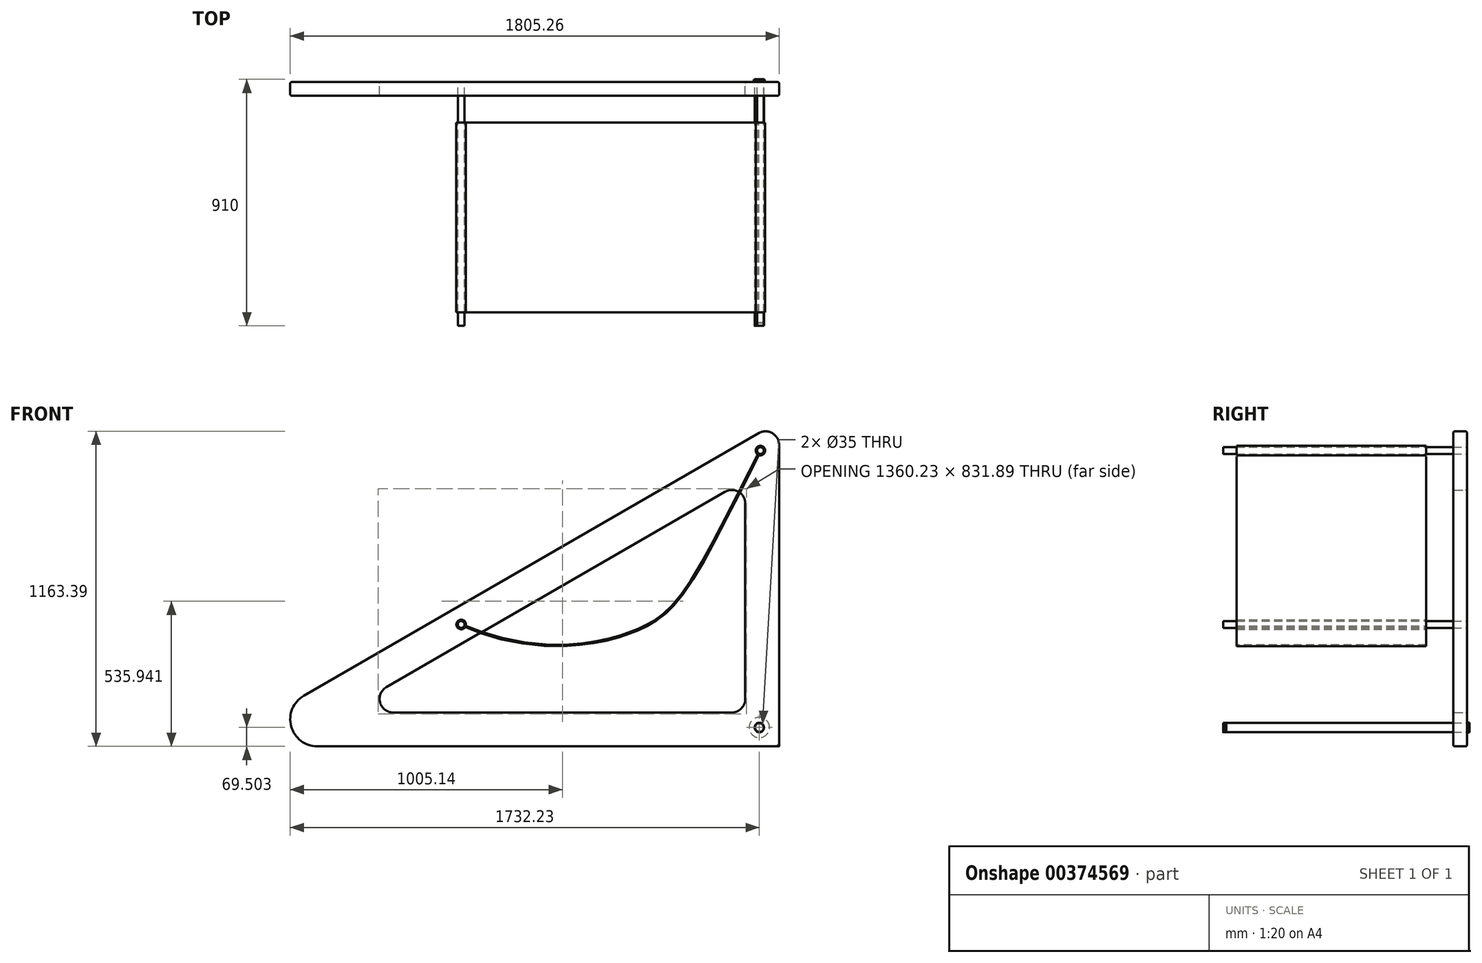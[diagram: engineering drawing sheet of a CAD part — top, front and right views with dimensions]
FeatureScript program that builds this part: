
annotation { "Feature Type Name" : "Feature", "Feature Type Description" : "" }
export const myFeature = defineFeature(function(context is Context, id is Id, definition is map)
    precondition{}
    {
        {
            var Q0;
            Q0=qCreatedBy(makeId("Front.planeOp"),FACE);
            var sketch = newSketch(context, id + "F0", { "sketchPlane" : qUnion([Q0])});
            skLineSegment(sketch, "E0.0", {"start": v(1202.53, -38.1) * mm, "end": v(2907.29, -38.1) * mm});
            skLineSegment(sketch, "E0.1", {"start": v(2832.79, 1118.6) * mm, "end": v(1152.53, 148.5) * mm});
            skLineSegment(sketch, "E0.2", {"start": v(2907.79, -37.6) * mm, "end": v(2907.79, 1075.3) * mm});
            skLineSegment(sketch, "E1.0", {"start": v(2782.79, 136.9) * mm, "end": v(2782.79, 858.8) * mm});
            skLineSegment(sketch, "E1.1", {"start": v(1482.43, 86.9) * mm, "end": v(2732.79, 86.9) * mm});
            skLineSegment(sketch, "E1.2", {"start": v(2707.79, 902.1) * mm, "end": v(1457.43, 180.2) * mm});
            skCircle(sketch, "E2", {"center": v(2838.8, 1054.2) * mm, "radius": 12.5 * mm});
            skCircle(sketch, "E3", {"center": v(2834.76, 31.41) * mm, "radius": 17.5 * mm});
            skCircle(sketch, "E4", {"center": v(1733.75, 411.9) * mm, "radius": 12.5 * mm});
            skCircle(sketch, "E5.cCircle", {"center": v(2838.8, 1054.2) * mm, "radius": 12.5 * mm, "construction": true});
            skLineSegment(sketch, "E5.0", {"start": v(2824.76, 1050.86) * mm, "end": v(2828.89, 1064.69) * mm});
            skLineSegment(sketch, "E5.1", {"start": v(2828.89, 1064.69) * mm, "end": v(2842.93, 1068.03) * mm});
            skLineSegment(sketch, "E5.2", {"start": v(2842.93, 1068.03) * mm, "end": v(2852.84, 1057.54) * mm});
            skLineSegment(sketch, "E5.3", {"start": v(2852.84, 1057.54) * mm, "end": v(2848.72, 1043.7) * mm});
            skLineSegment(sketch, "E5.4", {"start": v(2848.72, 1043.7) * mm, "end": v(2834.68, 1040.37) * mm});
            skLineSegment(sketch, "E5.5", {"start": v(2834.68, 1040.37) * mm, "end": v(2824.76, 1050.86) * mm});
            skPoint(sketch, "E5.0.midPoint", {"position": v(2826.82, 1057.77) * mm});
            skCircle(sketch, "E6.cCircle", {"center": v(2834.76, 31.41) * mm, "radius": 17.5 * mm, "construction": true});
            skLineSegment(sketch, "E6.0", {"start": v(2814.58, 30.3) * mm, "end": v(2823.7, 48.33) * mm});
            skLineSegment(sketch, "E6.1", {"start": v(2823.7, 48.33) * mm, "end": v(2843.88, 49.44) * mm});
            skLineSegment(sketch, "E6.2", {"start": v(2843.88, 49.44) * mm, "end": v(2854.93, 32.53) * mm});
            skLineSegment(sketch, "E6.3", {"start": v(2854.93, 32.53) * mm, "end": v(2845.81, 14.5) * mm});
            skLineSegment(sketch, "E6.4", {"start": v(2845.81, 14.5) * mm, "end": v(2825.63, 13.38) * mm});
            skLineSegment(sketch, "E6.5", {"start": v(2825.63, 13.38) * mm, "end": v(2814.58, 30.3) * mm});
            skPoint(sketch, "E6.0.midPoint", {"position": v(2819.14, 39.31) * mm});
            skCircle(sketch, "E7.cCircle", {"center": v(1733.75, 411.9) * mm, "radius": 12.5 * mm, "construction": true});
            skLineSegment(sketch, "E7.0", {"start": v(1721.66, 419.79) * mm, "end": v(1734.53, 426.32) * mm});
            skLineSegment(sketch, "E7.1", {"start": v(1734.53, 426.32) * mm, "end": v(1746.62, 418.43) * mm});
            skLineSegment(sketch, "E7.2", {"start": v(1746.62, 418.43) * mm, "end": v(1745.84, 404.02) * mm});
            skLineSegment(sketch, "E7.3", {"start": v(1745.84, 404.02) * mm, "end": v(1732.96, 397.5) * mm});
            skLineSegment(sketch, "E7.4", {"start": v(1732.96, 397.5) * mm, "end": v(1720.87, 405.38) * mm});
            skLineSegment(sketch, "E7.5", {"start": v(1720.87, 405.38) * mm, "end": v(1721.66, 419.79) * mm});
            skPoint(sketch, "E7.0.midPoint", {"position": v(1728.1, 423.05) * mm});
            skCircle(sketch, "E8", {"center": v(1733.75, 411.9) * mm, "radius": 37.5 * mm});
            skCircle(sketch, "E9", {"center": v(2838.8, 1054.2) * mm, "radius": 37.5 * mm});
            skCircle(sketch, "E10", {"center": v(2834.76, 31.41) * mm, "radius": 37.5 * mm});
            skPoint(sketch, "E11.visualSharp", {"position": v(829.32, -38.1) * mm});
            skArc(sketch, "E11.filletArc", {"start": v(1152.53, 148.5) * mm, "mid": v(1105.94, 36.02) * mm, "end": v(1202.53, -38.1) * mm});
            skPoint(sketch, "E12.visualSharp", {"position": v(1295.83, 86.9) * mm});
            skArc(sketch, "E12.filletArc", {"start": v(1457.43, 180.2) * mm, "mid": v(1434.14, 123.96) * mm, "end": v(1482.43, 86.9) * mm});
            skPoint(sketch, "E13.visualSharp", {"position": v(2782.79, 945.4) * mm});
            skArc(sketch, "E13.filletArc", {"start": v(2782.79, 858.8) * mm, "mid": v(2757.79, 902.1) * mm, "end": v(2707.79, 902.1) * mm});
            skPoint(sketch, "E14.visualSharp", {"position": v(2907.79, 1161.9) * mm});
            skArc(sketch, "E14.filletArc", {"start": v(2907.79, 1075.3) * mm, "mid": v(2882.79, 1118.6) * mm, "end": v(2832.79, 1118.6) * mm});
            skPoint(sketch, "E15.visualSharp", {"position": v(2782.79, 86.9) * mm});
            skArc(sketch, "E15.filletArc", {"start": v(2732.79, 86.9) * mm, "mid": v(2768.14, 101.55) * mm, "end": v(2782.79, 136.9) * mm});
            skPoint(sketch, "E16.visualSharp", {"position": v(2907.79, -38.1) * mm});
            skArc(sketch, "E16.filletArc", {"start": v(2907.29, -38.1) * mm, "mid": v(2907.64, -37.95) * mm, "end": v(2907.79, -37.6) * mm});
            skSolve(sketch);
        }
        {
            var Q0;
            Q0=makeQuery(id+"F0.imprint","IMPRINT",FACE,{"disambiguationData":[TD([[makeQuery(id+"F0.imprint","IMPRINT",EDGE,{"derivedFrom":sQuery(id+"F0.wireOp",EDGE,"E0.0")}),1.0]])]});
            var Q1;
            Q1=makeQuery(id+"F0.imprint","IMPRINT",FACE,{"disambiguationData":[TD([[makeQuery(id+"F0.imprint","IMPRINT",EDGE,{"derivedFrom":sQuery(id+"F0.wireOp",EDGE,"E9")}),1.0]])]});
            var Q2;
            {var subQ0=sQuery(id+"F0.wireOp",EDGE,"E5.4");var subQ1=sQuery(id+"F0.wireOp",EDGE,"E2");var subQ2=makeQuery(id+"F0.imprint","INTERSECT",VERTEX,{"derivedFrom":[subQ1,subQ0]});Q2=makeQuery(id+"F0.imprint","IMPRINT",FACE,{"disambiguationData":[TD([[makeQuery(id+"F0.imprint","IMPRINT",EDGE,{"disambiguationData":[TD([[subQ2,-1.0]])],"derivedFrom":subQ1}),-1.0]])]});}
            var Q3;
            {var subQ0=sQuery(id+"F0.wireOp",EDGE,"E5.2");var subQ1=sQuery(id+"F0.wireOp",EDGE,"E2");var subQ2=makeQuery(id+"F0.imprint","INTERSECT",VERTEX,{"derivedFrom":[subQ1,subQ0]});Q3=makeQuery(id+"F0.imprint","IMPRINT",FACE,{"disambiguationData":[TD([[makeQuery(id+"F0.imprint","IMPRINT",EDGE,{"disambiguationData":[TD([[subQ2,1.0]])],"derivedFrom":subQ1}),-1.0]])]});}
            var Q4;
            {var subQ0=sQuery(id+"F0.wireOp",EDGE,"E5.5");var subQ1=sQuery(id+"F0.wireOp",EDGE,"E2");var subQ2=makeQuery(id+"F0.imprint","INTERSECT",VERTEX,{"derivedFrom":[subQ1,subQ0]});Q4=makeQuery(id+"F0.imprint","IMPRINT",FACE,{"disambiguationData":[TD([[makeQuery(id+"F0.imprint","IMPRINT",EDGE,{"disambiguationData":[TD([[subQ2,-1.0]])],"derivedFrom":subQ1}),-1.0]])]});}
            var Q5;
            {var subQ0=sQuery(id+"F0.wireOp",EDGE,"E5.0");var subQ1=sQuery(id+"F0.wireOp",EDGE,"E2");var subQ2=makeQuery(id+"F0.imprint","INTERSECT",VERTEX,{"derivedFrom":[subQ1,subQ0]});Q5=makeQuery(id+"F0.imprint","IMPRINT",FACE,{"disambiguationData":[TD([[makeQuery(id+"F0.imprint","IMPRINT",EDGE,{"disambiguationData":[TD([[subQ2,-1.0]])],"derivedFrom":subQ1}),-1.0]])]});}
            var Q6;
            {var subQ0=sQuery(id+"F0.wireOp",EDGE,"E5.1");var subQ1=sQuery(id+"F0.wireOp",EDGE,"E2");var subQ2=makeQuery(id+"F0.imprint","INTERSECT",VERTEX,{"derivedFrom":[subQ1,subQ0]});Q6=makeQuery(id+"F0.imprint","IMPRINT",FACE,{"disambiguationData":[TD([[makeQuery(id+"F0.imprint","IMPRINT",EDGE,{"disambiguationData":[TD([[subQ2,-1.0]])],"derivedFrom":subQ1}),-1.0]])]});}
            var Q7;
            {var subQ0=sQuery(id+"F0.wireOp",EDGE,"E5.1");var subQ1=sQuery(id+"F0.wireOp",EDGE,"E2");var subQ2=makeQuery(id+"F0.imprint","INTERSECT",VERTEX,{"derivedFrom":[subQ1,subQ0]});Q7=makeQuery(id+"F0.imprint","IMPRINT",FACE,{"disambiguationData":[TD([[makeQuery(id+"F0.imprint","IMPRINT",EDGE,{"disambiguationData":[TD([[subQ2,1.0]])],"derivedFrom":subQ1}),-1.0]])]});}
            var Q8;
            Q8=makeQuery(id+"F0.imprint","IMPRINT",FACE,{"disambiguationData":[TD([[makeQuery(id+"F0.imprint","IMPRINT",EDGE,{"derivedFrom":sQuery(id+"F0.wireOp",EDGE,"E10")}),1.0]])]});
            var Q9;
            {var subQ0=sQuery(id+"F0.wireOp",EDGE,"E6.2");var subQ1=sQuery(id+"F0.wireOp",EDGE,"E3");var subQ2=makeQuery(id+"F0.imprint","INTERSECT",VERTEX,{"derivedFrom":[subQ1,subQ0]});Q9=makeQuery(id+"F0.imprint","IMPRINT",FACE,{"disambiguationData":[TD([[makeQuery(id+"F0.imprint","IMPRINT",EDGE,{"disambiguationData":[TD([[subQ2,1.0]])],"derivedFrom":subQ1}),-1.0]])]});}
            var Q10;
            {var subQ0=sQuery(id+"F0.wireOp",EDGE,"E6.1");var subQ1=sQuery(id+"F0.wireOp",EDGE,"E3");var subQ2=makeQuery(id+"F0.imprint","INTERSECT",VERTEX,{"derivedFrom":[subQ1,subQ0]});Q10=makeQuery(id+"F0.imprint","IMPRINT",FACE,{"disambiguationData":[TD([[makeQuery(id+"F0.imprint","IMPRINT",EDGE,{"disambiguationData":[TD([[subQ2,-1.0]])],"derivedFrom":subQ1}),-1.0]])]});}
            var Q11;
            {var subQ0=sQuery(id+"F0.wireOp",EDGE,"E6.1");var subQ1=sQuery(id+"F0.wireOp",EDGE,"E3");var subQ2=makeQuery(id+"F0.imprint","INTERSECT",VERTEX,{"derivedFrom":[subQ1,subQ0]});Q11=makeQuery(id+"F0.imprint","IMPRINT",FACE,{"disambiguationData":[TD([[makeQuery(id+"F0.imprint","IMPRINT",EDGE,{"disambiguationData":[TD([[subQ2,1.0]])],"derivedFrom":subQ1}),-1.0]])]});}
            var Q12;
            {var subQ0=sQuery(id+"F0.wireOp",EDGE,"E6.4");var subQ1=sQuery(id+"F0.wireOp",EDGE,"E3");var subQ2=makeQuery(id+"F0.imprint","INTERSECT",VERTEX,{"derivedFrom":[subQ1,subQ0]});Q12=makeQuery(id+"F0.imprint","IMPRINT",FACE,{"disambiguationData":[TD([[makeQuery(id+"F0.imprint","IMPRINT",EDGE,{"disambiguationData":[TD([[subQ2,-1.0]])],"derivedFrom":subQ1}),-1.0]])]});}
            var Q13;
            {var subQ0=sQuery(id+"F0.wireOp",EDGE,"E6.5");var subQ1=sQuery(id+"F0.wireOp",EDGE,"E3");var subQ2=makeQuery(id+"F0.imprint","INTERSECT",VERTEX,{"derivedFrom":[subQ1,subQ0]});Q13=makeQuery(id+"F0.imprint","IMPRINT",FACE,{"disambiguationData":[TD([[makeQuery(id+"F0.imprint","IMPRINT",EDGE,{"disambiguationData":[TD([[subQ2,-1.0]])],"derivedFrom":subQ1}),-1.0]])]});}
            var Q14;
            {var subQ0=sQuery(id+"F0.wireOp",EDGE,"E6.0");var subQ1=sQuery(id+"F0.wireOp",EDGE,"E3");var subQ2=makeQuery(id+"F0.imprint","INTERSECT",VERTEX,{"derivedFrom":[subQ1,subQ0]});Q14=makeQuery(id+"F0.imprint","IMPRINT",FACE,{"disambiguationData":[TD([[makeQuery(id+"F0.imprint","IMPRINT",EDGE,{"disambiguationData":[TD([[subQ2,-1.0]])],"derivedFrom":subQ1}),-1.0]])]});}
            var Q15;
            Q15=makeQuery(id+"F0.imprint","IMPRINT",FACE,{"disambiguationData":[TD([[makeQuery(id+"F0.imprint","IMPRINT",EDGE,{"derivedFrom":sQuery(id+"F0.wireOp",EDGE,"E8")}),1.0]])]});
            var Q16;
            {var subQ0=sQuery(id+"F0.wireOp",EDGE,"E7.0");var subQ1=sQuery(id+"F0.wireOp",EDGE,"E4");var subQ2=makeQuery(id+"F0.imprint","INTERSECT",VERTEX,{"derivedFrom":[subQ1,subQ0]});Q16=makeQuery(id+"F0.imprint","IMPRINT",FACE,{"disambiguationData":[TD([[makeQuery(id+"F0.imprint","IMPRINT",EDGE,{"disambiguationData":[TD([[subQ2,1.0]])],"derivedFrom":subQ1}),-1.0]])]});}
            var Q17;
            {var subQ0=sQuery(id+"F0.wireOp",EDGE,"E7.3");var subQ1=sQuery(id+"F0.wireOp",EDGE,"E4");var subQ2=makeQuery(id+"F0.imprint","INTERSECT",VERTEX,{"derivedFrom":[subQ1,subQ0]});Q17=makeQuery(id+"F0.imprint","IMPRINT",FACE,{"disambiguationData":[TD([[makeQuery(id+"F0.imprint","IMPRINT",EDGE,{"disambiguationData":[TD([[subQ2,-1.0]])],"derivedFrom":subQ1}),-1.0]])]});}
            var Q18;
            {var subQ0=sQuery(id+"F0.wireOp",EDGE,"E7.1");var subQ1=sQuery(id+"F0.wireOp",EDGE,"E4");var subQ2=makeQuery(id+"F0.imprint","INTERSECT",VERTEX,{"derivedFrom":[subQ1,subQ0]});Q18=makeQuery(id+"F0.imprint","IMPRINT",FACE,{"disambiguationData":[TD([[makeQuery(id+"F0.imprint","IMPRINT",EDGE,{"disambiguationData":[TD([[subQ2,1.0]])],"derivedFrom":subQ1}),-1.0]])]});}
            var Q19;
            {var subQ0=sQuery(id+"F0.wireOp",EDGE,"E7.4");var subQ1=sQuery(id+"F0.wireOp",EDGE,"E4");var subQ2=makeQuery(id+"F0.imprint","INTERSECT",VERTEX,{"derivedFrom":[subQ1,subQ0]});Q19=makeQuery(id+"F0.imprint","IMPRINT",FACE,{"disambiguationData":[TD([[makeQuery(id+"F0.imprint","IMPRINT",EDGE,{"disambiguationData":[TD([[subQ2,-1.0]])],"derivedFrom":subQ1}),-1.0]])]});}
            var Q20;
            {var subQ0=sQuery(id+"F0.wireOp",EDGE,"E7.0");var subQ1=sQuery(id+"F0.wireOp",EDGE,"E4");var subQ2=makeQuery(id+"F0.imprint","INTERSECT",VERTEX,{"derivedFrom":[subQ1,subQ0]});Q20=makeQuery(id+"F0.imprint","IMPRINT",FACE,{"disambiguationData":[TD([[makeQuery(id+"F0.imprint","IMPRINT",EDGE,{"disambiguationData":[TD([[subQ2,-1.0]])],"derivedFrom":subQ1}),-1.0]])]});}
            var Q21;
            {var subQ0=sQuery(id+"F0.wireOp",EDGE,"E7.5");var subQ1=sQuery(id+"F0.wireOp",EDGE,"E4");var subQ2=makeQuery(id+"F0.imprint","INTERSECT",VERTEX,{"derivedFrom":[subQ1,subQ0]});Q21=makeQuery(id+"F0.imprint","IMPRINT",FACE,{"disambiguationData":[TD([[makeQuery(id+"F0.imprint","IMPRINT",EDGE,{"disambiguationData":[TD([[subQ2,-1.0]])],"derivedFrom":subQ1}),-1.0]])]});}
            extrude(context, id + "F1", {"entities" : qUnion([Q0, Q1, Q2, Q3, Q4, Q5, Q6, Q7, Q8, Q9, Q10, Q11, Q12, Q13, Q14, Q15, Q16, Q17, Q18, Q19, Q20, Q21]), "depth" : 50 * mm});
        }
        {
            var Q0;
            Q0=makeQuery(id+"F0.imprint","IMPRINT",FACE,{"disambiguationData":[TD([[makeQuery(id+"F0.imprint","IMPRINT",EDGE,{"derivedFrom":sQuery(id+"F0.wireOp",EDGE,"E2")}),1.0]])]});
            var Q1;
            Q1=makeQuery(id+"F0.imprint","IMPRINT",FACE,{"disambiguationData":[TD([[makeQuery(id+"F0.imprint","IMPRINT",EDGE,{"derivedFrom":sQuery(id+"F0.wireOp",EDGE,"E3")}),1.0]])]});
            var Q2;
            Q2=makeQuery(id+"F0.imprint","IMPRINT",FACE,{"disambiguationData":[TD([[makeQuery(id+"F0.imprint","IMPRINT",EDGE,{"derivedFrom":sQuery(id+"F0.wireOp",EDGE,"E4")}),1.0]])]});
            extrude(context, id + "F2", {"entities" : qUnion([Q0, Q1, Q2]), "depth" : 25 * 36 * mm});
        }
        {
            var Q0;
            Q0=makeQuery(id+"F1.opExtrude","CAP_FACE",FACE,{"disambiguationData":[OSD([sQuery(id+"F0.wireOp",EDGE,"E0.0"),sQuery(id+"F0.wireOp",EDGE,"E0.1"),sQuery(id+"F0.wireOp",EDGE,"E0.2"),sQuery(id+"F0.wireOp",EDGE,"E1.0"),sQuery(id+"F0.wireOp",EDGE,"E1.1"),sQuery(id+"F0.wireOp",EDGE,"E1.2"),sQuery(id+"F0.wireOp",EDGE,"E2"),sQuery(id+"F0.wireOp",EDGE,"E3"),sQuery(id+"F0.wireOp",EDGE,"E4")])],"isStart":false});
            var sketch = newSketch(context, id + "F3", { "sketchPlane" : qUnion([Q0])});
            skFitSpline(sketch, "E17", {"points": [v(1733.75, 411.9) * mm, v(2383.9, 392.1) * mm, v(2838.8, 1054.2) * mm], "startDerivative": vector(1756.38, -743.3) * mm, "endDerivative": vector(1453.35, 2857.32) * mm});
            skCircle(sketch, "E18", {"center": v(1733.75, 411.9) * mm, "radius": 12.73 * mm});
            skCircle(sketch, "E19", {"center": v(2838.8, 1054.2) * mm, "radius": 12.64 * mm});
            skCircle(sketch, "E20.0", {"center": v(1733.75, 411.9) * mm, "radius": 17.73 * mm});
            skFitSpline(sketch, "E21.0", {"points": [v(1732.77, 409.6) * mm, v(1769.45, 394.08) * mm, v(1841.23, 368.44) * mm, v(1943.57, 344.38) * mm, v(2039.9, 332.88) * mm, v(2114.66, 332.24) * mm, v(2170.83, 336.19) * mm, v(2211.05, 341.14) * mm, v(2249.3, 347.86) * mm, v(2285.48, 356.12) * mm, v(2319.52, 365.7) * mm, v(2346.04, 374.57) * mm, v(2366.1, 382.1) * mm, v(2380.58, 387.93) * mm, v(2394.45, 393.9) * mm, v(2412.2, 402.13) * mm, v(2433.13, 413.04) * mm, v(2456.63, 427.63) * mm, v(2478.9, 444.17) * mm, v(2500.34, 463.15) * mm, v(2521.33, 485) * mm, v(2549.28, 518.63) * mm, v(2585.15, 570.22) * mm, v(2632.98, 651.24) * mm, v(2688.9, 755.21) * mm, v(2756.16, 885.96) * mm, v(2810.75, 993.54) * mm, v(2841.03, 1053.07) * mm]});
            skFitSpline(sketch, "E22.0", {"points": [v(1734.72, 414.2) * mm, v(1771.23, 398.76) * mm, v(1842.66, 373.25) * mm, v(1944.45, 349.31) * mm, v(2040.23, 337.88) * mm, v(2114.53, 337.25) * mm, v(2170.35, 341.17) * mm, v(2210.31, 346.09) * mm, v(2248.3, 352.77) * mm, v(2284.24, 360.97) * mm, v(2318.05, 370.47) * mm, v(2344.38, 379.29) * mm, v(2364.3, 386.76) * mm, v(2376.26, 391.58) * mm, v(2385.53, 395.5) * mm, v(2394.6, 399.5) * mm, v(2405.6, 404.58) * mm, v(2418.26, 410.93) * mm, v(2434.52, 419.8) * mm, v(2453.82, 431.77) * mm, v(2475.74, 448.06) * mm, v(2496.86, 466.75) * mm, v(2517.6, 488.33) * mm, v(2545.26, 521.61) * mm, v(2580.9, 572.88) * mm, v(2628.6, 653.67) * mm, v(2684.46, 757.52) * mm, v(2751.7, 888.23) * mm, v(2806.3, 995.8) * mm, v(2836.57, 1055.33) * mm]});
            skCircle(sketch, "E23.0", {"center": v(2838.8, 1054.2) * mm, "radius": 17.64 * mm});
            skSolve(sketch);
        }
        {
            var Q0;
            Q0 = qSketchRegion(id + "F3", true);
            extrude(context, id + "F4", {"entities" : qUnion([Q0]), "depth" : (25 * 32) * mm});
        }
        {
            var Q0;
            Q0 = qSketchRegion(id + "F3", true);
            extrude(context, id + "F5", {"entities" : qUnion([Q0]), "operationType" : NewBodyOperationType.REMOVE, "depth" : 100 * mm});
        }
        {
            var Q0;
            Q0=makeQuery(id+"F0.imprint","IMPRINT",FACE,{"disambiguationData":[TD([[makeQuery(id+"F0.imprint","IMPRINT",EDGE,{"derivedFrom":sQuery(id+"F0.wireOp",EDGE,"E10")}),1.0]])]});
            var Q1;
            Q1=makeQuery(id+"F2.opExtrude","CAP_FACE",FACE,{"disambiguationData":[OSD([sQuery(id+"F0.wireOp",EDGE,"E3")])],"isStart":true});
            var Q2;
            {var subQ0=sQuery(id+"F0.wireOp",EDGE,"E6.1");var subQ1=sQuery(id+"F0.wireOp",EDGE,"E3");var subQ2=makeQuery(id+"F0.imprint","INTERSECT",VERTEX,{"derivedFrom":[subQ1,subQ0]});Q2=makeQuery(id+"F0.imprint","IMPRINT",FACE,{"disambiguationData":[TD([[makeQuery(id+"F0.imprint","IMPRINT",EDGE,{"disambiguationData":[TD([[subQ2,1.0]])],"derivedFrom":subQ1}),-1.0]])]});}
            var Q3;
            {var subQ0=sQuery(id+"F0.wireOp",EDGE,"E6.4");var subQ1=sQuery(id+"F0.wireOp",EDGE,"E3");var subQ2=makeQuery(id+"F0.imprint","INTERSECT",VERTEX,{"derivedFrom":[subQ1,subQ0]});Q3=makeQuery(id+"F0.imprint","IMPRINT",FACE,{"disambiguationData":[TD([[makeQuery(id+"F0.imprint","IMPRINT",EDGE,{"disambiguationData":[TD([[subQ2,-1.0]])],"derivedFrom":subQ1}),-1.0]])]});}
            var Q4;
            {var subQ0=sQuery(id+"F0.wireOp",EDGE,"E6.1");var subQ1=sQuery(id+"F0.wireOp",EDGE,"E3");var subQ2=makeQuery(id+"F0.imprint","INTERSECT",VERTEX,{"derivedFrom":[subQ1,subQ0]});Q4=makeQuery(id+"F0.imprint","IMPRINT",FACE,{"disambiguationData":[TD([[makeQuery(id+"F0.imprint","IMPRINT",EDGE,{"disambiguationData":[TD([[subQ2,-1.0]])],"derivedFrom":subQ1}),-1.0]])]});}
            var Q5;
            {var subQ0=sQuery(id+"F0.wireOp",EDGE,"E6.0");var subQ1=sQuery(id+"F0.wireOp",EDGE,"E3");var subQ2=makeQuery(id+"F0.imprint","INTERSECT",VERTEX,{"derivedFrom":[subQ1,subQ0]});Q5=makeQuery(id+"F0.imprint","IMPRINT",FACE,{"disambiguationData":[TD([[makeQuery(id+"F0.imprint","IMPRINT",EDGE,{"disambiguationData":[TD([[subQ2,-1.0]])],"derivedFrom":subQ1}),-1.0]])]});}
            var Q6;
            {var subQ0=sQuery(id+"F0.wireOp",EDGE,"E6.2");var subQ1=sQuery(id+"F0.wireOp",EDGE,"E3");var subQ2=makeQuery(id+"F0.imprint","INTERSECT",VERTEX,{"derivedFrom":[subQ1,subQ0]});Q6=makeQuery(id+"F0.imprint","IMPRINT",FACE,{"disambiguationData":[TD([[makeQuery(id+"F0.imprint","IMPRINT",EDGE,{"disambiguationData":[TD([[subQ2,1.0]])],"derivedFrom":subQ1}),-1.0]])]});}
            var Q7;
            Q7=makeQuery(id+"F2.opExtrude","CAP_FACE",FACE,{"disambiguationData":[OSD([sQuery(id+"F0.wireOp",EDGE,"E3")])],"isStart":false});
            var Q8;
            {var subQ0=sQuery(id+"F0.wireOp",EDGE,"E6.5");var subQ1=sQuery(id+"F0.wireOp",EDGE,"E3");var subQ2=makeQuery(id+"F0.imprint","INTERSECT",VERTEX,{"derivedFrom":[subQ1,subQ0]});Q8=makeQuery(id+"F0.imprint","IMPRINT",FACE,{"disambiguationData":[TD([[makeQuery(id+"F0.imprint","IMPRINT",EDGE,{"disambiguationData":[TD([[subQ2,-1.0]])],"derivedFrom":subQ1}),-1.0]])]});}
            extrude(context, id + "F6", {"entities" : qUnion([Q0, Q1, Q2, Q3, Q4, Q5, Q6, Q7, Q8]), "oppositeDirection" : true, "depth" : 1 * mm});
        }
        {
            var Q0;
            {var subQ0=sQuery(id+"F0.wireOp",EDGE,"E6.4");var subQ1=sQuery(id+"F0.wireOp",EDGE,"E3");var subQ2=makeQuery(id+"F0.imprint","INTERSECT",VERTEX,{"derivedFrom":[subQ1,subQ0]});Q0=makeQuery(id+"F0.imprint","IMPRINT",FACE,{"disambiguationData":[TD([[makeQuery(id+"F0.imprint","IMPRINT",EDGE,{"disambiguationData":[TD([[subQ2,-1.0]])],"derivedFrom":subQ1}),-1.0]])]});}
            var Q1;
            {var subQ0=sQuery(id+"F0.wireOp",EDGE,"E6.2");var subQ1=sQuery(id+"F0.wireOp",EDGE,"E3");var subQ2=makeQuery(id+"F0.imprint","INTERSECT",VERTEX,{"derivedFrom":[subQ1,subQ0]});Q1=makeQuery(id+"F0.imprint","IMPRINT",FACE,{"disambiguationData":[TD([[makeQuery(id+"F0.imprint","IMPRINT",EDGE,{"disambiguationData":[TD([[subQ2,1.0]])],"derivedFrom":subQ1}),-1.0]])]});}
            var Q2;
            {var subQ0=sQuery(id+"F0.wireOp",EDGE,"E6.1");var subQ1=sQuery(id+"F0.wireOp",EDGE,"E3");var subQ2=makeQuery(id+"F0.imprint","INTERSECT",VERTEX,{"derivedFrom":[subQ1,subQ0]});Q2=makeQuery(id+"F0.imprint","IMPRINT",FACE,{"disambiguationData":[TD([[makeQuery(id+"F0.imprint","IMPRINT",EDGE,{"disambiguationData":[TD([[subQ2,-1.0]])],"derivedFrom":subQ1}),-1.0]])]});}
            var Q3;
            {var subQ0=sQuery(id+"F0.wireOp",EDGE,"E6.1");var subQ1=sQuery(id+"F0.wireOp",EDGE,"E3");var subQ2=makeQuery(id+"F0.imprint","INTERSECT",VERTEX,{"derivedFrom":[subQ1,subQ0]});Q3=makeQuery(id+"F0.imprint","IMPRINT",FACE,{"disambiguationData":[TD([[makeQuery(id+"F0.imprint","IMPRINT",EDGE,{"disambiguationData":[TD([[subQ2,1.0]])],"derivedFrom":subQ1}),-1.0]])]});}
            var Q4;
            {var subQ0=sQuery(id+"F0.wireOp",EDGE,"E3");var subQ4=makeQuery(id+"F0.imprint","INTERSECT",VERTEX,{"derivedFrom":[subQ0,sQuery(id+"F0.wireOp",EDGE,"E6.1")]});Q4=makeQuery(id+"F0.imprint","IMPRINT",FACE,{"disambiguationData":[TD([[makeQuery(id+"F0.imprint","IMPRINT",EDGE,{"disambiguationData":[TD([[subQ4,1.0]])],"derivedFrom":subQ0}),1.0]])]});}
            var Q5;
            {var subQ0=sQuery(id+"F0.wireOp",EDGE,"E6.0");var subQ1=sQuery(id+"F0.wireOp",EDGE,"E3");var subQ2=makeQuery(id+"F0.imprint","INTERSECT",VERTEX,{"derivedFrom":[subQ1,subQ0]});Q5=makeQuery(id+"F0.imprint","IMPRINT",FACE,{"disambiguationData":[TD([[makeQuery(id+"F0.imprint","IMPRINT",EDGE,{"disambiguationData":[TD([[subQ2,-1.0]])],"derivedFrom":subQ1}),-1.0]])]});}
            var Q6;
            {var subQ0=sQuery(id+"F0.wireOp",EDGE,"E3");Q6=makeQuery(id+"F6.opExtrude","CAP_FACE",FACE,{"disambiguationData":[OSD([subQ0]),TDD([makeQuery(id+"F2.opExtrude","CAP_FACE",FACE,{"disambiguationData":[OSD([subQ0])],"isStart":true})])],"isStart":true});}
            var Q7;
            Q7=makeQuery(id+"F2.opExtrude","CAP_FACE",FACE,{"disambiguationData":[OSD([sQuery(id+"F0.wireOp",EDGE,"E3")])],"isStart":true});
            var Q8;
            {var subQ0=sQuery(id+"F0.wireOp",EDGE,"E6.5");var subQ1=sQuery(id+"F0.wireOp",EDGE,"E3");var subQ2=makeQuery(id+"F0.imprint","INTERSECT",VERTEX,{"derivedFrom":[subQ1,subQ0]});Q8=makeQuery(id+"F0.imprint","IMPRINT",FACE,{"disambiguationData":[TD([[makeQuery(id+"F0.imprint","IMPRINT",EDGE,{"disambiguationData":[TD([[subQ2,-1.0]])],"derivedFrom":subQ1}),-1.0]])]});}
            var Q9;
            {var subQ0=sQuery(id+"F0.wireOp",EDGE,"E3");Q9=makeQuery(id+"F6.opExtrude","CAP_FACE",FACE,{"disambiguationData":[OSD([subQ0]),TDD([makeQuery(id+"F2.opExtrude","CAP_FACE",FACE,{"disambiguationData":[OSD([subQ0])],"isStart":false})])],"isStart":false});}
            var Q10;
            Q10=makeQuery(id+"F2.opExtrude","CAP_FACE",FACE,{"disambiguationData":[OSD([sQuery(id+"F0.wireOp",EDGE,"E3")])],"isStart":false});
            var Q11;
            {var subQ0=sQuery(id+"F0.wireOp",EDGE,"E3");Q11=makeQuery(id+"F6.opExtrude","CAP_FACE",FACE,{"disambiguationData":[OSD([subQ0]),TDD([makeQuery(id+"F2.opExtrude","CAP_FACE",FACE,{"disambiguationData":[OSD([subQ0])],"isStart":false})])],"isStart":true});}
            extrude(context, id + "F7", {"entities" : qUnion([Q0, Q1, Q2, Q3, Q4, Q5, Q6, Q7, Q8, Q9, Q10, Q11]), "oppositeDirection" : true, "depth" : (10) * mm});
        }
        {
            var Q0;
            Q0=makeQuery(id+"F1.opExtrude","CAP_EDGE",EDGE,{"disambiguationData":[OSD([sQuery(id+"F0.wireOp",EDGE,"E0.1")])],"isStart":false});
            var Q1;
            Q1=makeQuery(id+"F1.opExtrude","CAP_EDGE",EDGE,{"disambiguationData":[OSD([sQuery(id+"F0.wireOp",EDGE,"E14.filletArc")])],"isStart":false});
            var Q2;
            Q2=makeQuery(id+"F1.opExtrude","CAP_EDGE",EDGE,{"disambiguationData":[OSD([sQuery(id+"F0.wireOp",EDGE,"E0.2")])],"isStart":true});
            var Q3;
            Q3=makeQuery(id+"F1.opExtrude","CAP_EDGE",EDGE,{"disambiguationData":[OSD([sQuery(id+"F0.wireOp",EDGE,"E13.filletArc")])],"isStart":true});
            var Q4;
            Q4=makeQuery(id+"F1.opExtrude","CAP_EDGE",EDGE,{"disambiguationData":[OSD([sQuery(id+"F0.wireOp",EDGE,"E1.1")])],"isStart":false});
            fillet(context, id + "F8", {"entities" : qUnion([Q0, Q1, Q2, Q3, Q4]), "radius" : 5 * mm, "tangentPropagation" : true, "allowEdgeOverflow" : false});
        }
        {
            var Q0;
            Q0=makeQuery(id+"F7.opExtrude","CAP_EDGE",EDGE,{"disambiguationData":[OSD([sQuery(id+"F0.wireOp",EDGE,"E6.1")])],"isStart":false});
            var Q1;
            Q1=makeQuery(id+"F7.opExtrude","CAP_EDGE",EDGE,{"disambiguationData":[OSD([sQuery(id+"F0.wireOp",EDGE,"E6.2")])],"isStart":false});
            var Q2;
            Q2=makeQuery(id+"F7.opExtrude","CAP_EDGE",EDGE,{"disambiguationData":[OSD([sQuery(id+"F0.wireOp",EDGE,"E6.3")])],"isStart":false});
            var Q3;
            Q3=makeQuery(id+"F7.opExtrude","CAP_EDGE",EDGE,{"disambiguationData":[OSD([sQuery(id+"F0.wireOp",EDGE,"E6.4")])],"isStart":false});
            var Q4;
            Q4=makeQuery(id+"F7.opExtrude","CAP_EDGE",EDGE,{"disambiguationData":[OSD([sQuery(id+"F0.wireOp",EDGE,"E6.5")])],"isStart":false});
            var Q5;
            Q5=makeQuery(id+"F7.opExtrude","CAP_EDGE",EDGE,{"disambiguationData":[OSD([sQuery(id+"F0.wireOp",EDGE,"E6.0")])],"isStart":false});
            chamfer(context, id + "F9", {"entities" : qUnion([Q0, Q1, Q2, Q3, Q4, Q5]), "chamferType" : ChamferType.TWO_OFFSETS, "width1" : 5 * mm, "oppositeDirection" : false, "width2" : 1 * mm, "tangentPropagation" : true});
        }
    });
